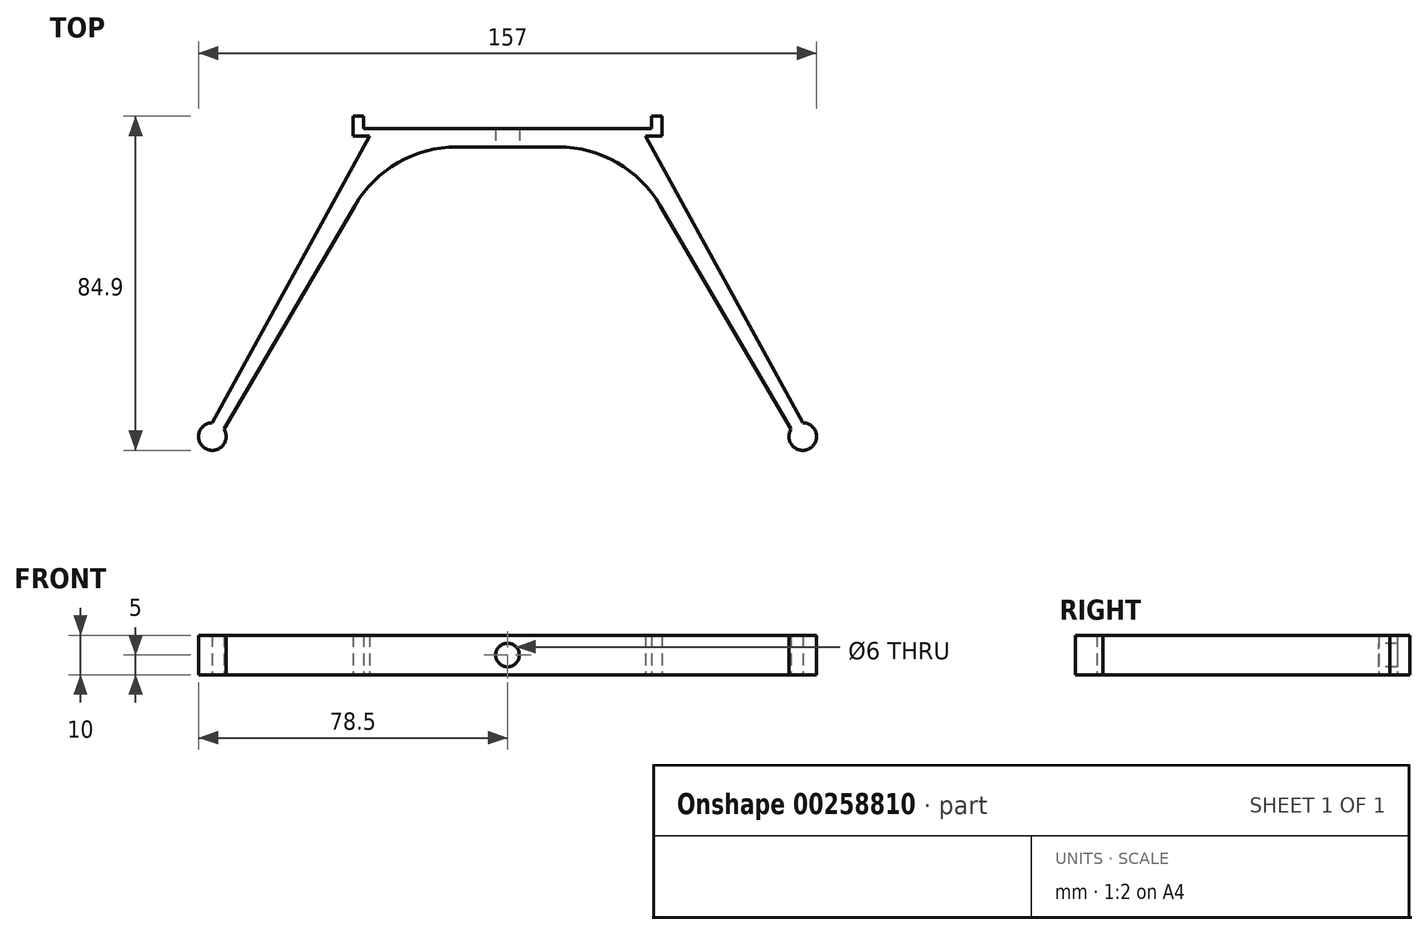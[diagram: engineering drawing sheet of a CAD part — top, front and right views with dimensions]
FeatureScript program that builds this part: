
annotation { "Feature Type Name" : "Feature", "Feature Type Description" : "" }
export const myFeature = defineFeature(function(context is Context, id is Id, definition is map)
    precondition{}
    {
        {
            var Q0;
            Q0=qCreatedBy(makeId("Top.planeOp"),FACE);
            var sketch = newSketch(context, id + "F0", { "sketchPlane" : qUnion([Q0])});
            skLineSegment(sketch, "E0.bottom", {"start": v(75, -37.5) * mm, "end": v(-75, -37.5) * mm, "construction": true});
            skLineSegment(sketch, "E0.top", {"start": v(75, 37.5) * mm, "end": v(-75, 37.5) * mm, "construction": true});
            skLineSegment(sketch, "E0.left", {"start": v(75, -37.5) * mm, "end": v(75, 37.5) * mm, "construction": true});
            skLineSegment(sketch, "E0.right", {"start": v(-75, -37.5) * mm, "end": v(-75, 37.5) * mm, "construction": true});
            skPoint(sketch, "E0.middle", {"position": v(0, 0) * mm});
            skArc(sketch, "E1", {"start": v(-75, -34) * mm, "mid": v(-76.68, -40.57) * mm, "end": v(-72.05, -35.62) * mm});
            skArc(sketch, "E2", {"start": v(72.05, -35.62) * mm, "mid": v(76.68, -40.57) * mm, "end": v(75, -34) * mm});
            skLineSegment(sketch, "E3.bottom", {"start": v(30.1, 36.1) * mm, "end": v(-30.1, 36.1) * mm});
            skLineSegment(sketch, "E3.top", {"start": v(35, 38.9) * mm, "end": v(-35, 38.9) * mm});
            skPoint(sketch, "E3.middle", {"position": v(0, 37.5) * mm});
            skLineSegment(sketch, "E4", {"start": v(-35, 38.9) * mm, "end": v(-75, -34) * mm});
            skLineSegment(sketch, "E5", {"start": v(0, 45.65) * mm, "end": v(0, -44.51) * mm, "construction": true});
            skLineSegment(sketch, "E6", {"start": v(-72.05, -35.62) * mm, "end": v(-30.1, 36.1) * mm});
            skLineSegment(sketch, "E7.MirrorCS", {"start": v(72.05, -35.62) * mm, "end": v(30.1, 36.1) * mm});
            skLineSegment(sketch, "E8.MirrorCS", {"start": v(35, 38.9) * mm, "end": v(75, -34) * mm});
            skPoint(sketch, "E9.orphan", {"position": v(35, 36.1) * mm});
            skPoint(sketch, "E10.orphan", {"position": v(-35, 36.1) * mm});
            skSolve(sketch);
        }
        {
            var Q0;
            Q0 = qSketchRegion(id + "F0", true);
            extrude(context, id + "F1", {"entities" : qUnion([Q0]), "depth" : 10 * mm});
        }
        {
            var Q0;
            Q0=makeQuery(id+"F1.opExtrude","SWEPT_EDGE",EDGE,{"disambiguationData":[OSD([sQuery(id+"F0.wireOp",EDGE,"E3.bottom"),sQuery(id+"F0.wireOp",EDGE,"E6")])]});
            var Q1;
            Q1=makeQuery(id+"F1.opExtrude","SWEPT_EDGE",EDGE,{"disambiguationData":[OSD([sQuery(id+"F0.wireOp",EDGE,"E3.bottom"),sQuery(id+"F0.wireOp",EDGE,"E7.MirrorCS")])]});
            fillet(context, id + "F2", {"entities" : qUnion([Q0, Q1]), "radius" : 30 * mm, "tangentPropagation" : true, "allowEdgeOverflow" : false});
        }
        {
            var Q0;
            Q0=makeQuery(id+"F1.opExtrude","SWEPT_FACE",FACE,{"disambiguationData":[OSD([sQuery(id+"F0.wireOp",EDGE,"E3.top")])]});
            var sketch = newSketch(context, id + "F3", { "sketchPlane" : qUnion([Q0])});
            skLineSegment(sketch, "E11.bottom", {"start": v(-39.29, 10) * mm, "end": v(39.29, 10) * mm});
            skLineSegment(sketch, "E11.top", {"start": v(-39.29, 0) * mm, "end": v(39.29, 0) * mm});
            skLineSegment(sketch, "E11.left", {"start": v(-39.29, 10) * mm, "end": v(-39.29, 0) * mm});
            skLineSegment(sketch, "E11.right", {"start": v(39.29, 10) * mm, "end": v(39.29, 0) * mm});
            skPoint(sketch, "E11.middle", {"position": v(0, 5) * mm});
            skPoint(sketch, "E11.middle.positionSnap0", {"position": v(35, 5) * mm});
            skPoint(sketch, "E11.centerSnap0", {"position": v(35, 5) * mm});
            skSolve(sketch);
        }
        {
            var Q0;
            Q0 = qSketchRegion(id + "F3", true);
            extrude(context, id + "F4", {"entities" : qUnion([Q0]), "operationType" : NewBodyOperationType.ADD, "depth" : 5 * mm});
        }
        {
            var Q0;
            Q0=makeQuery(id+"F4.opExtrude","CAP_FACE",FACE,{"disambiguationData":[OSD([sQuery(id+"F3.wireOp",EDGE,"E11.bottom"),sQuery(id+"F3.wireOp",EDGE,"E11.top"),sQuery(id+"F3.wireOp",EDGE,"E11.left"),sQuery(id+"F3.wireOp",EDGE,"E11.right")])],"isStart":false});
            var sketch = newSketch(context, id + "F5", { "sketchPlane" : qUnion([Q0])});
            skLineSegment(sketch, "E12.bottom", {"start": v(-36.52, 10) * mm, "end": v(36.52, 10) * mm});
            skLineSegment(sketch, "E12.top", {"start": v(-36.52, 0) * mm, "end": v(36.52, 0) * mm});
            skLineSegment(sketch, "E12.left", {"start": v(-36.52, 10) * mm, "end": v(-36.52, 0) * mm});
            skLineSegment(sketch, "E12.right", {"start": v(36.52, 10) * mm, "end": v(36.52, 0) * mm});
            skPoint(sketch, "E12.middle", {"position": v(0, 5) * mm});
            skPoint(sketch, "E12.middle.positionSnap0", {"position": v(39.29, 5) * mm});
            skPoint(sketch, "E12.centerSnap0", {"position": v(39.29, 5) * mm});
            skSolve(sketch);
        }
        {
            var Q0;
            Q0 = qSketchRegion(id + "F5", true);
            extrude(context, id + "F6", {"entities" : qUnion([Q0]), "operationType" : NewBodyOperationType.REMOVE, "oppositeDirection" : true, "depth" : 3.2 * mm});
        }
        {
            var Q0;
            Q0=makeQuery(id+"F1.opExtrude","SWEPT_FACE",FACE,{"disambiguationData":[OSD([sQuery(id+"F0.wireOp",EDGE,"E3.bottom")])]});
            var sketch = newSketch(context, id + "F7", { "sketchPlane" : qUnion([Q0])});
            skCircle(sketch, "E13", {"center": v(0, 5) * mm, "radius": 3 * mm});
            skPoint(sketch, "E13.centerSnap0", {"position": v(-12.89, 5) * mm});
            skSolve(sketch);
        }
        {
            var Q0;
            Q0 = qSketchRegion(id + "F7", true);
            extrude(context, id + "F8", {"entities" : qUnion([Q0]), "operationType" : NewBodyOperationType.REMOVE, "endBound" : BoundingType.THROUGH_ALL, "oppositeDirection" : true, "depth" : 25 * mm});
        }
    });
